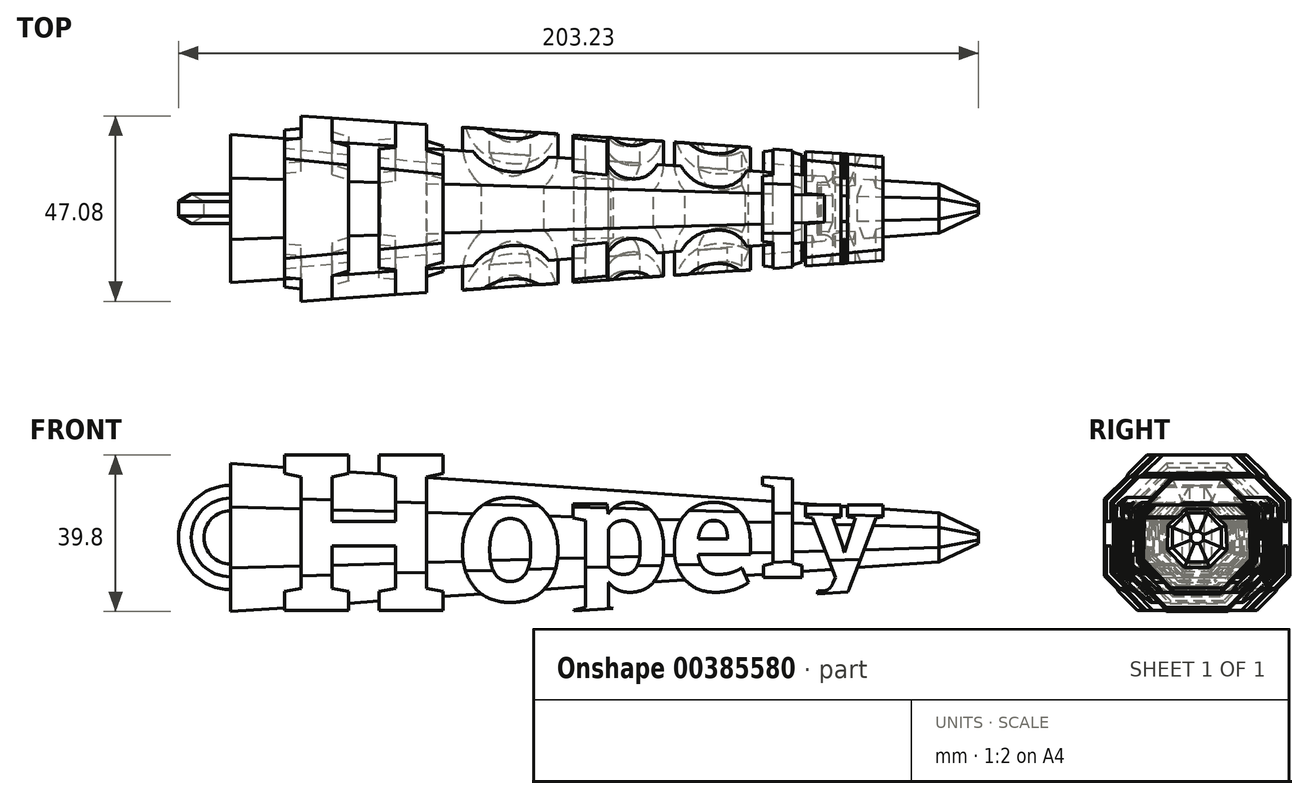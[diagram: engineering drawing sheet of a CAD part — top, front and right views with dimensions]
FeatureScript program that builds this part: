
annotation { "Feature Type Name" : "Feature", "Feature Type Description" : "" }
export const myFeature = defineFeature(function(context is Context, id is Id, definition is map)
    precondition{}
    {
        {
            assignVariable(context, id + "F0", {"name" : "hookPlane", "anyValue" : 90});
        }
        {
            assignVariable(context, id + "F1", {"name" : "halfLength", "anyValue" : 90});
        }
        {
            var Q0;
            Q0=qCreatedBy(makeId("Front.planeOp"),FACE);
            var sketch = newSketch(context, id + "F2", { "sketchPlane" : qUnion([Q0])});
            skText(sketch, "E0", { "text": "H", "fontName": "RobotoSlab-Bold.ttf"});
            skPoint(sketch, "E1", {"position": v(-32.57, 0) * mm});
            skText(sketch, "E2", { "text": "o", "fontName": "RobotoSlab-Bold.ttf"});
            skText(sketch, "E3", { "text": "pe", "fontName": "RobotoSlab-Bold.ttf"});
            skText(sketch, "E4", { "text": "ly", "fontName": "RobotoSlab-Bold.ttf"});
            skPoint(sketch, "E5", {"position": v(-3.86, 0) * mm});
            skPoint(sketch, "E6", {"position": v(44.6, 0.9) * mm});
            skLineSegment(sketch, "E7", {"start": v(-77.85, -20) * mm, "end": v(-77.85, -51.65) * mm, "construction": true});
            skLineSegment(sketch, "E8", {"start": v(-77.85, -51.65) * mm, "end": v(77.85, -51.65) * mm, "construction": true});
            skLineSegment(sketch, "E9", {"start": v(77.85, -51.65) * mm, "end": v(77.85, -11.6) * mm, "construction": true});
            skPoint(sketch, "E10", {"position": v(0, -51.65) * mm});
            skPoint(sketch, "E11", {"position": v(44.6, 0) * mm});
            const initialGuessF2  = {"E0": [-0.07785, -0.02, 1, 0, 0.04], "E2": [-0.03257, -0.0175, 1, 0, 0.035], "E3": [-0.00386, -0.015, 1, 0, 0.03], "E4": [0.0446, -0.0116, 1, 0, 0.025]};
            skSetInitialGuess(sketch, initialGuessF2);
            skSolve(sketch);
        }
        {
            var Q0;
            Q0=qSketchRegion(id+"F2",true);
            extrude(context, id + "F3", {"entities" : qUnion([Q0]), "depth" : 25 * mm, "hasSecondDirection" : true, "secondDirectionOppositeDirection" : true, "secondDirectionDepth" : 25 * mm});
        }
        {
            var Q0;
            Q0=qCreatedBy(makeId("Right.planeOp"),FACE);
            var sketch = newSketch(context, id + "F4", { "sketchPlane" : qUnion([Q0])});
            skCircle(sketch, "E12", {"center": v(0, -1.5) * mm, "radius": 12.5 * mm, "construction": true});
            skLineSegment(sketch, "E13", {"start": v(0, 19.5) * mm, "end": v(0, 13.15) * mm, "construction": true});
            skLineSegment(sketch, "E14.0", {"start": v(-5.18, 11) * mm, "end": v(5.18, 11) * mm});
            skLineSegment(sketch, "E14.1", {"start": v(5.18, 11) * mm, "end": v(12.5, 3.67) * mm});
            skLineSegment(sketch, "E14.2", {"start": v(12.5, 3.67) * mm, "end": v(12.5, -6.68) * mm});
            skLineSegment(sketch, "E14.3", {"start": v(12.5, -6.68) * mm, "end": v(5.18, -14) * mm});
            skLineSegment(sketch, "E14.4", {"start": v(5.18, -14) * mm, "end": v(-5.18, -14) * mm});
            skLineSegment(sketch, "E14.5", {"start": v(-5.18, -14) * mm, "end": v(-12.5, -6.68) * mm});
            skLineSegment(sketch, "E14.6", {"start": v(-12.5, -6.68) * mm, "end": v(-12.5, 3.67) * mm});
            skLineSegment(sketch, "E14.7", {"start": v(-12.5, 3.67) * mm, "end": v(-5.18, 11) * mm});
            skPoint(sketch, "E14.0.midPoint", {"position": v(0, 11) * mm});
            skLineSegment(sketch, "E15", {"start": v(0, 19.5) * mm, "end": v(0, 11) * mm});
            skSolve(sketch);
        }
        {
            var Q0;
            Q0=qSketchRegion(id+"F4",true);
            var Q1;
            Q1=makeQuery(id+"F3.opExtrude","SWEPT_FACE",FACE,{"disambiguationData":[OSD([sQuery(id+"F2.wireOp",EDGE,"E4.sketch_text.stroke-1")])]});
            extrude(context, id + "F5", {"entities" : qUnion([Q0]), "operationType" : NewBodyOperationType.ADD, "oppositeDirection" : true, "depth" : (getVariable(context, 'halfLength')) * mm, "hasDraft" : true, "draftAngle" : 4 * degree, "hasSecondDirection" : true, "secondDirectionOppositeDirection" : false, "secondDirectionBoundEntityFace" : qUnion([Q1]), "secondDirectionDepth" : (getVariable(context, 'halfLength')) * mm, "hasSecondDirectionDraft" : true, "secondDirectionDraftAngle" : 4 * degree, "secondDirectionDraftPullDirection" : true});
        }
        {
            var Q0;
            Q0=qCreatedBy(makeId("Right.planeOp"),FACE);
            var sketch = newSketch(context, id + "F6", { "sketchPlane" : qUnion([Q0])});
            skCircle(sketch, "E16.cCircle", {"center": v(0, -1.5) * mm, "radius": 18.5 * mm, "construction": true});
            skLineSegment(sketch, "E16.0", {"start": v(-7.66, 17) * mm, "end": v(7.66, 17) * mm});
            skLineSegment(sketch, "E16.1", {"start": v(7.66, 17) * mm, "end": v(18.5, 6.16) * mm});
            skLineSegment(sketch, "E16.2", {"start": v(18.5, 6.16) * mm, "end": v(18.5, -9.17) * mm});
            skLineSegment(sketch, "E16.3", {"start": v(18.5, -9.17) * mm, "end": v(7.66, -20) * mm});
            skLineSegment(sketch, "E16.4", {"start": v(7.66, -20) * mm, "end": v(-7.66, -20) * mm});
            skLineSegment(sketch, "E16.5", {"start": v(-7.66, -20) * mm, "end": v(-18.5, -9.17) * mm});
            skLineSegment(sketch, "E16.6", {"start": v(-18.5, -9.17) * mm, "end": v(-18.5, 6.16) * mm});
            skLineSegment(sketch, "E16.7", {"start": v(-18.5, 6.16) * mm, "end": v(-7.66, 17) * mm});
            skLineSegment(sketch, "E17.bottom", {"start": v(37.5, 36) * mm, "end": v(-37.5, 36) * mm});
            skLineSegment(sketch, "E17.top", {"start": v(37.5, -39) * mm, "end": v(-37.5, -39) * mm});
            skLineSegment(sketch, "E17.left", {"start": v(37.5, 36) * mm, "end": v(37.5, -39) * mm});
            skLineSegment(sketch, "E17.right", {"start": v(-37.5, 36) * mm, "end": v(-37.5, -39) * mm});
            skLineSegment(sketch, "E18", {"start": v(0, 19.5) * mm, "end": v(0, -8.52) * mm, "construction": true});
            skSolve(sketch);
        }
        {
            var Q0;
            Q0=makeQuery(id+"F6.imprint","IMPRINT",FACE,{"disambiguationData":[TD([[makeQuery(id+"F6.imprint","IMPRINT",EDGE,{"derivedFrom":sQuery(id+"F6.wireOp",EDGE,"E16.0")}),1.0]])]});
            extrude(context, id + "F7", {"entities" : qUnion([Q0]), "operationType" : NewBodyOperationType.REMOVE, "endBound" : BoundingType.THROUGH_ALL, "depth" : 25 * mm, "hasDraft" : true, "draftAngle" : 4 * degree, "hasSecondDirection" : true, "secondDirectionBound" : SecondDirectionBoundingType.THROUGH_ALL, "secondDirectionOppositeDirection" : true, "secondDirectionDepth" : 25 * mm, "hasSecondDirectionDraft" : true, "secondDirectionDraftAngle" : 4 * degree, "secondDirectionDraftPullDirection" : true});
        }
        {
            var Q0;
            {var subQ0=sQuery(id+"F4.wireOp",EDGE,"E14.3");var subQ1=sQuery(id+"F4.wireOp",EDGE,"E14.2");var subQ2=sQuery(id+"F4.wireOp",EDGE,"E14.4");var subQ3=sQuery(id+"F4.wireOp",EDGE,"E14.5");var subQ4=sQuery(id+"F4.wireOp",EDGE,"E14.6");Q0=makeQuery(id+"F5.boolean.opBoolean","SPLIT",FACE,{"disambiguationData":[TD([makeQuery(id+"F3.opExtrude","SWEPT_FACE",FACE,{"disambiguationData":[OSD([sQuery(id+"F2.wireOp",EDGE,"E4.sketch_text.stroke-0")])]})])],"derivedFrom":makeQuery(id+"F5.opExtrude","CAP_FACE",FACE,{"disambiguationData":[OSD([sQuery(id+"F4.wireOp",EDGE,"E14.0"),sQuery(id+"F4.wireOp",EDGE,"E14.1"),subQ1,subQ0,subQ2,subQ3,subQ4,sQuery(id+"F4.wireOp",EDGE,"E14.7")])],"isStart":true})});}
            var sketch = newSketch(context, id + "F8", { "sketchPlane" : qUnion([Q0])});
            skCircle(sketch, "E19.cCircle", {"center": v(0, -1.5) * mm, "radius": 6.2 * mm, "construction": true});
            skLineSegment(sketch, "E19.0", {"start": v(-2.57, 4.7) * mm, "end": v(2.57, 4.7) * mm});
            skLineSegment(sketch, "E19.1", {"start": v(2.57, 4.7) * mm, "end": v(6.2, 1.07) * mm});
            skLineSegment(sketch, "E19.2", {"start": v(6.2, 1.07) * mm, "end": v(6.2, -4.07) * mm});
            skLineSegment(sketch, "E19.3", {"start": v(6.2, -4.07) * mm, "end": v(2.57, -7.71) * mm});
            skLineSegment(sketch, "E19.4", {"start": v(2.57, -7.71) * mm, "end": v(-2.57, -7.71) * mm});
            skLineSegment(sketch, "E19.5", {"start": v(-2.57, -7.71) * mm, "end": v(-6.2, -4.07) * mm});
            skLineSegment(sketch, "E19.6", {"start": v(-6.2, -4.07) * mm, "end": v(-6.2, 1.07) * mm});
            skLineSegment(sketch, "E19.7", {"start": v(-6.2, 1.07) * mm, "end": v(-2.57, 4.7) * mm});
            skPoint(sketch, "E19.0.midPoint", {"position": v(0, 4.7) * mm});
            skLineSegment(sketch, "E20", {"start": v(0, 19.59) * mm, "end": v(0, -20.57) * mm, "construction": true});
            skSolve(sketch);
        }
        {
            var Q0;
            Q0=qSketchRegion(id+"F8",true);
            extrude(context, id + "F9", {"entities" : qUnion([Q0]), "operationType" : NewBodyOperationType.ADD, "depth" : 10 * mm, "hasDraft" : true, "draftAngle" : 25 * degree, "draftPullDirection" : true});
        }
        {
            var Q0;
            Q0=qCreatedBy(makeId("Right.planeOp"),FACE);
            cPlane(context, id + "F10", {"entities" : qUnion([Q0]), "cplaneType" : CPlaneType.OFFSET, "offset" : (getVariable(context, 'hookPlane')) * mm, "oppositeDirection" : true, "width" : 150 * mm, "height" : 150 * mm});
        }
        {
            var Q0;
            Q0=qCreatedBy(makeId("Front.planeOp"),FACE);
            var sketch = newSketch(context, id + "F11", { "sketchPlane" : qUnion([Q0])});
            skArc(sketch, "E21", {"start": v(-83.39, 6) * mm, "mid": v(-100, -1.5) * mm, "end": v(-83.39, -9) * mm});
            skLineSegment(sketch, "E22", {"start": v(-83.39, 6) * mm, "end": v(-83.39, -9) * mm, "construction": true});
            skPoint(sketch, "E23", {"position": v(-83.39, -1.5) * mm});
            skLineSegment(sketch, "E24", {"start": v(-90, 17.29) * mm, "end": v(-90, -20.3) * mm, "construction": true});
            skSolve(sketch);
        }
        {
            var Q0;
            Q0=qCreatedBy(id+"F10.planeOp",FACE);
            var sketch = newSketch(context, id + "F12", { "sketchPlane" : qUnion([Q0])});
            skCircle(sketch, "E25.cCircle", {"center": v(0, 8.5) * mm, "radius": 3.23 * mm, "construction": true});
            skLineSegment(sketch, "E25.0", {"start": v(1.87, 5.26) * mm, "end": v(-1.87, 5.26) * mm});
            skLineSegment(sketch, "E25.1", {"start": v(-1.87, 5.26) * mm, "end": v(-3.73, 8.5) * mm});
            skLineSegment(sketch, "E25.2", {"start": v(-3.73, 8.5) * mm, "end": v(-1.87, 11.73) * mm});
            skLineSegment(sketch, "E25.3", {"start": v(-1.87, 11.73) * mm, "end": v(1.87, 11.73) * mm});
            skLineSegment(sketch, "E25.4", {"start": v(1.87, 11.73) * mm, "end": v(3.73, 8.5) * mm});
            skLineSegment(sketch, "E25.5", {"start": v(3.73, 8.5) * mm, "end": v(1.87, 5.26) * mm});
            skPoint(sketch, "E25.0.midPoint", {"position": v(0, 5.26) * mm});
            skSolve(sketch);
        }
        {
            var Q0;
            Q0=qSketchRegion(id+"F12",true);
            var Q1;
            Q1=qConstructionFilter(qBodyType(qCreatedBy(id+"F11",EDGE),BodyType.WIRE),ConstructionObject.NO);
            sweep(context, id + "F13", {"operationType" : NewBodyOperationType.ADD, "profiles" : qUnion([Q0]), "path" : qUnion([Q1])});
        }
    });
